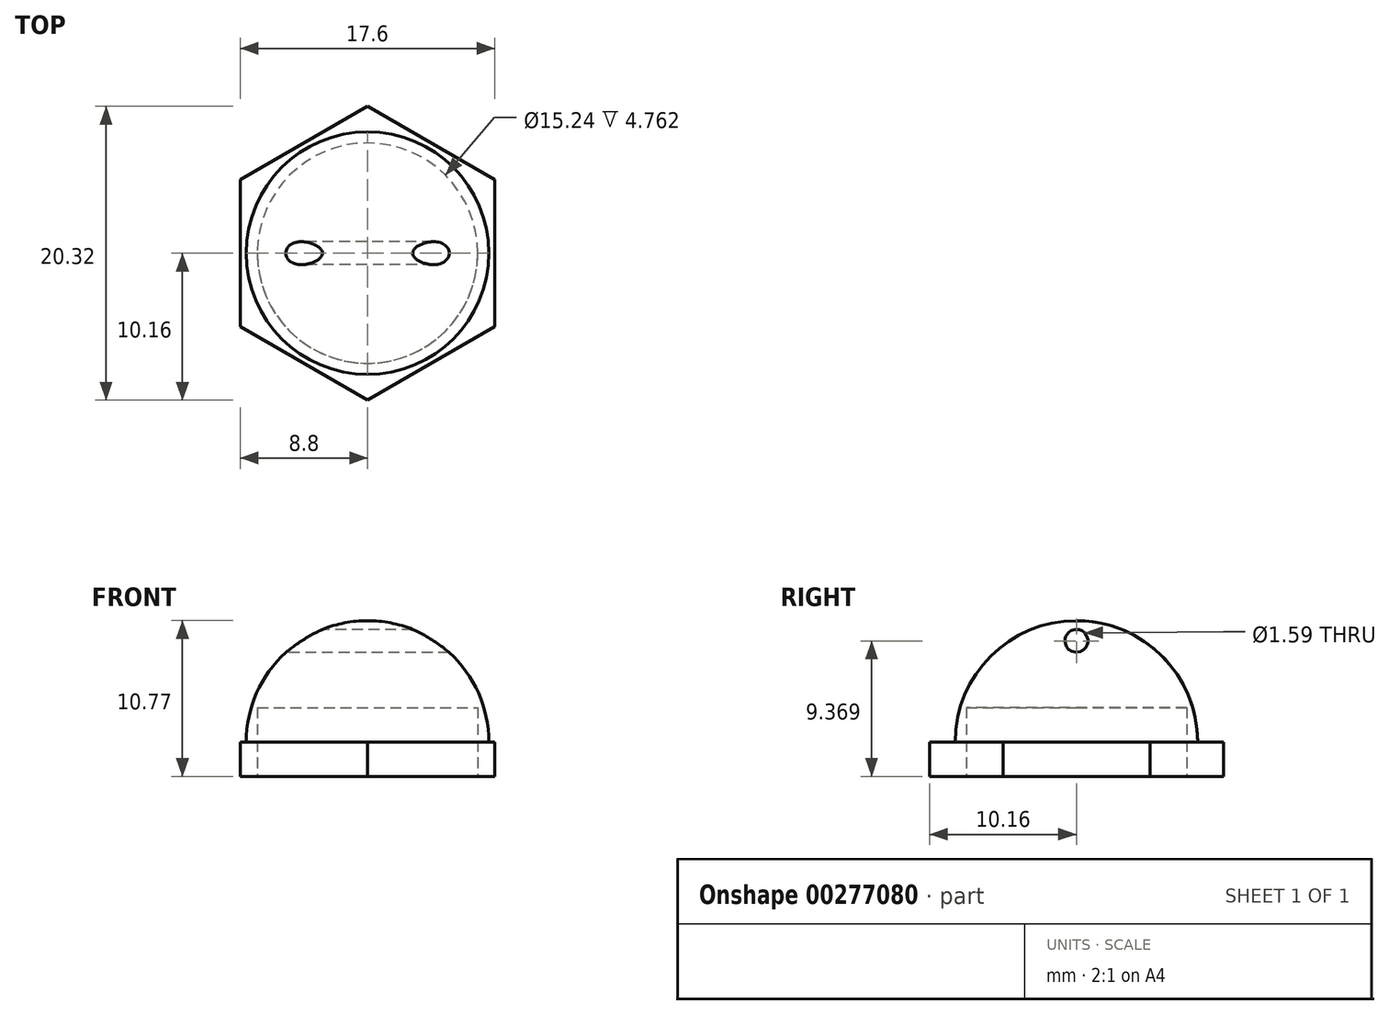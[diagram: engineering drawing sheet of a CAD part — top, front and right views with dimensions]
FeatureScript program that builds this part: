
annotation { "Feature Type Name" : "Feature", "Feature Type Description" : "" }
export const myFeature = defineFeature(function(context is Context, id is Id, definition is map)
    precondition{}
    {
        {
            var Q0;
            Q0=qCreatedBy(makeId("Top.planeOp"),FACE);
            var sketch = newSketch(context, id + "F0", { "sketchPlane" : qUnion([Q0])});
            skCircle(sketch, "E0.cCircle", {"center": v(0, 0) * mm, "radius": 10.16 * mm, "construction": true});
            skLineSegment(sketch, "E0.0", {"start": v(0, 10.16) * mm, "end": v(8.8, 5.08) * mm});
            skLineSegment(sketch, "E0.1", {"start": v(8.8, 5.08) * mm, "end": v(8.8, -5.08) * mm});
            skLineSegment(sketch, "E0.2", {"start": v(8.8, -5.08) * mm, "end": v(0, -10.16) * mm});
            skLineSegment(sketch, "E0.3", {"start": v(0, -10.16) * mm, "end": v(-8.8, -5.08) * mm});
            skLineSegment(sketch, "E0.4", {"start": v(-8.8, -5.08) * mm, "end": v(-8.8, 5.08) * mm});
            skLineSegment(sketch, "E0.5", {"start": v(-8.8, 5.08) * mm, "end": v(0, 10.16) * mm});
            skSolve(sketch);
        }
        {
            var Q0;
            Q0=qSketchRegion(id+"F0",true);
            extrude(context, id + "F1", {"entities" : qUnion([Q0]), "depth" : 7.94 * mm});
        }
        {
            var Q0;
            Q0=makeQuery(id+"F1.opExtrude","CAP_FACE",FACE,{"disambiguationData":[OSD([sQuery(id+"F0.wireOp",EDGE,"E0.0"),sQuery(id+"F0.wireOp",EDGE,"E0.1"),sQuery(id+"F0.wireOp",EDGE,"E0.2"),sQuery(id+"F0.wireOp",EDGE,"E0.3"),sQuery(id+"F0.wireOp",EDGE,"E0.4"),sQuery(id+"F0.wireOp",EDGE,"E0.5")])],"isStart":false});
            var sketch = newSketch(context, id + "F2", { "sketchPlane" : qUnion([Q0])});
            skCircle(sketch, "E1.cCircle", {"center": v(0, 0) * mm, "radius": 8.26 * mm, "construction": true});
            skLineSegment(sketch, "E1.0", {"start": v(0, 8.26) * mm, "end": v(1.27, 7.52) * mm});
            skLineSegment(sketch, "E1.1", {"start": v(7.15, 4.13) * mm, "end": v(7.15, 2.66) * mm});
            skLineSegment(sketch, "E1.2", {"start": v(7.15, -4.13) * mm, "end": v(5.88, -4.86) * mm});
            skLineSegment(sketch, "E1.3", {"start": v(0, -8.26) * mm, "end": v(-1.27, -7.52) * mm});
            skLineSegment(sketch, "E1.4", {"start": v(-7.15, -4.13) * mm, "end": v(-7.15, -2.66) * mm});
            skLineSegment(sketch, "E1.5", {"start": v(-7.15, 4.13) * mm, "end": v(-5.88, 4.86) * mm});
            skLineSegment(sketch, "E2", {"start": v(-1.27, 7.52) * mm, "end": v(1.27, 7.52) * mm});
            skLineSegment(sketch, "E3", {"start": v(-5.88, 4.86) * mm, "end": v(-7.15, 2.66) * mm});
            skLineSegment(sketch, "E4", {"start": v(-7.15, -2.66) * mm, "end": v(-5.88, -4.86) * mm});
            skLineSegment(sketch, "E5", {"start": v(-1.27, -7.52) * mm, "end": v(1.27, -7.52) * mm});
            skLineSegment(sketch, "E6", {"start": v(5.88, -4.86) * mm, "end": v(7.15, -2.66) * mm});
            skLineSegment(sketch, "E7", {"start": v(7.15, 2.66) * mm, "end": v(5.88, 4.86) * mm});
            skLineSegment(sketch, "E8.trimOffspring", {"start": v(-7.15, 2.66) * mm, "end": v(-7.15, 4.13) * mm});
            skLineSegment(sketch, "E9.trimOffspring", {"start": v(-5.88, -4.86) * mm, "end": v(-7.15, -4.13) * mm});
            skLineSegment(sketch, "E10.trimOffspring", {"start": v(1.27, -7.52) * mm, "end": v(0, -8.25) * mm});
            skLineSegment(sketch, "E11.trimOffspring", {"start": v(7.15, -2.66) * mm, "end": v(7.15, -4.13) * mm});
            skLineSegment(sketch, "E12.trimOffspring", {"start": v(5.88, 4.86) * mm, "end": v(7.15, 4.13) * mm});
            skLineSegment(sketch, "E13.trimOffspring", {"start": v(-1.27, 7.52) * mm, "end": v(0, 8.25) * mm});
            skCircle(sketch, "E14", {"center": v(0, 0) * mm, "radius": 7.52 * mm, "construction": true});
            skSolve(sketch);
        }
        {
            var Q0;
            Q0=qSketchRegion(id+"F2",true);
            extrude(context, id + "F3", {"entities" : qUnion([Q0]), "operationType" : NewBodyOperationType.ADD, "depth" : 22.22 * mm});
        }
        {
            var Q0;
            Q0=makeQuery(id+"F3.opExtrude","CAP_FACE",FACE,{"disambiguationData":[OSD([sQuery(id+"F2.wireOp",EDGE,"E1.0"),sQuery(id+"F2.wireOp",EDGE,"E2"),sQuery(id+"F2.wireOp",EDGE,"E13.trimOffspring")])],"isStart":false});
            var sketch = newSketch(context, id + "F4", { "sketchPlane" : qUnion([Q0])});
            skCircle(sketch, "E15.cCircle", {"center": v(0, 0) * mm, "radius": 10.16 * mm, "construction": true});
            skLineSegment(sketch, "E15.0", {"start": v(0, 10.16) * mm, "end": v(8.8, 5.08) * mm});
            skLineSegment(sketch, "E15.1", {"start": v(8.8, 5.08) * mm, "end": v(8.8, -5.08) * mm});
            skLineSegment(sketch, "E15.2", {"start": v(8.8, -5.08) * mm, "end": v(0, -10.16) * mm});
            skLineSegment(sketch, "E15.3", {"start": v(0, -10.16) * mm, "end": v(-8.8, -5.08) * mm});
            skLineSegment(sketch, "E15.4", {"start": v(-8.8, -5.08) * mm, "end": v(-8.8, 5.08) * mm});
            skLineSegment(sketch, "E15.5", {"start": v(-8.8, 5.08) * mm, "end": v(0, 10.16) * mm});
            skCircle(sketch, "E16", {"center": v(0, 0) * mm, "radius": 7.62 * mm});
            skSolve(sketch);
        }
        {
            var Q0;
            Q0=qSketchRegion(id+"F4",true);
            extrude(context, id + "F5", {"entities" : qUnion([Q0]), "operationType" : NewBodyOperationType.ADD, "depth" : 2.38 * mm});
        }
        {
            var Q0;
            Q0=qCreatedBy(makeId("Right.planeOp"),FACE);
            var sketch = newSketch(context, id + "F6", { "sketchPlane" : qUnion([Q0])});
            skLineSegment(sketch, "E17", {"start": v(0, 34.93) * mm, "end": v(-7.62, 34.93) * mm});
            skLineSegment(sketch, "E18", {"start": v(-7.62, 34.93) * mm, "end": v(-7.62, 32.54) * mm});
            skArc(sketch, "E19", {"start": v(0, 40.93) * mm, "mid": v(-5.93, 38.47) * mm, "end": v(-8.38, 32.54) * mm});
            skLineSegment(sketch, "E20", {"start": v(0, 40.93) * mm, "end": v(0, 34.93) * mm});
            skLineSegment(sketch, "E21", {"start": v(-8.38, 32.54) * mm, "end": v(-7.62, 32.54) * mm});
            skSolve(sketch);
        }
        {
            var Q0;
            Q0=qSketchRegion(id+"F6",true);
            var Q1;
            Q1=makeQuery(id+"F5.opExtrude","CAP_EDGE",EDGE,{"disambiguationData":[OSD([sQuery(id+"F4.wireOp",EDGE,"E16")])],"isStart":false});
            revolve(context, id + "F7", {"operationType" : NewBodyOperationType.ADD, "entities" : qUnion([Q0]), "axis" : qUnion([Q1]), "revolveType" : RevolveType.FULL});
        }
        {
            var Q0;
            Q0=makeQuery(id+"F1.opExtrude","CAP_FACE",FACE,{"disambiguationData":[OSD([sQuery(id+"F0.wireOp",EDGE,"E0.0"),sQuery(id+"F0.wireOp",EDGE,"E0.1"),sQuery(id+"F0.wireOp",EDGE,"E0.2"),sQuery(id+"F0.wireOp",EDGE,"E0.3"),sQuery(id+"F0.wireOp",EDGE,"E0.4"),sQuery(id+"F0.wireOp",EDGE,"E0.5")])],"isStart":true});
            var sketch = newSketch(context, id + "F8", { "sketchPlane" : qUnion([Q0])});
            skCircle(sketch, "E22", {"center": v(0, 0) * mm, "radius": 6.8 * mm});
            skSolve(sketch);
        }
        {
            var Q0;
            Q0=qSketchRegion(id+"F8",true);
            extrude(context, id + "F9", {"entities" : qUnion([Q0]), "operationType" : NewBodyOperationType.REMOVE, "oppositeDirection" : true, "depth" : 4.76 * mm});
        }
        {
            var Q0;
            Q0=makeQuery(id+"F9.boolean.opBoolean","COPY",FACE,{"derivedFrom":makeQuery(id+"F9.opExtrude","CAP_FACE",FACE,{"disambiguationData":[OSD([sQuery(id+"F8.wireOp",EDGE,"E22")])],"isStart":false})});
            var sketch = newSketch(context, id + "F10", { "sketchPlane" : qUnion([Q0])});
            skCircle(sketch, "E23", {"center": v(0, 0) * mm, "radius": 6.35 * mm});
            skSolve(sketch);
        }
        {
            var Q0;
            Q0=qSketchRegion(id+"F10",true);
            extrude(context, id + "F11", {"entities" : qUnion([Q0]), "operationType" : NewBodyOperationType.REMOVE, "endBound" : BoundingType.UP_TO_NEXT, "oppositeDirection" : true, "depth" : 25.4 * mm});
        }
        {
            var Q0;
            Q0=makeQuery(id+"F1.opExtrude","CAP_FACE",FACE,{"disambiguationData":[OSD([sQuery(id+"F0.wireOp",EDGE,"E0.0"),sQuery(id+"F0.wireOp",EDGE,"E0.1"),sQuery(id+"F0.wireOp",EDGE,"E0.2"),sQuery(id+"F0.wireOp",EDGE,"E0.3"),sQuery(id+"F0.wireOp",EDGE,"E0.4"),sQuery(id+"F0.wireOp",EDGE,"E0.5")])],"isStart":true});
            var sketch = newSketch(context, id + "F12", { "sketchPlane" : qUnion([Q0])});
            skCircle(sketch, "E24", {"center": v(0, 0) * mm, "radius": 6.8 * mm});
            skCircle(sketch, "E25.cCircle", {"center": v(0, 0) * mm, "radius": 8.57 * mm, "construction": true});
            skLineSegment(sketch, "E25.0", {"start": v(0, -8.57) * mm, "end": v(-7.42, -4.29) * mm});
            skLineSegment(sketch, "E25.1", {"start": v(-7.42, -4.29) * mm, "end": v(-7.42, 4.29) * mm});
            skLineSegment(sketch, "E25.2", {"start": v(-7.42, 4.29) * mm, "end": v(0, 8.57) * mm});
            skLineSegment(sketch, "E25.3", {"start": v(0, 8.57) * mm, "end": v(7.42, 4.29) * mm});
            skLineSegment(sketch, "E25.4", {"start": v(7.42, 4.29) * mm, "end": v(7.42, -4.29) * mm});
            skLineSegment(sketch, "E25.5", {"start": v(7.42, -4.29) * mm, "end": v(0, -8.57) * mm});
            skSolve(sketch);
        }
        {
            var Q0;
            Q0=qSketchRegion(id+"F12",true);
            extrude(context, id + "F13", {"entities" : qUnion([Q0]), "operationType" : NewBodyOperationType.ADD, "depth" : 3.17 * mm});
        }
        {
            var Q0;
            Q0=qCreatedBy(makeId("Right.planeOp"),FACE);
            var sketch = newSketch(context, id + "F14", { "sketchPlane" : qUnion([Q0])});
            skCircle(sketch, "E26", {"center": v(0, 39.53) * mm, "radius": 0.8 * mm});
            skSolve(sketch);
        }
        {
            var Q0;
            Q0=qSketchRegion(id+"F14",true);
            extrude(context, id + "F15", {"entities" : qUnion([Q0]), "operationType" : NewBodyOperationType.REMOVE, "endBound" : BoundingType.THROUGH_ALL, "depth" : 0.8 * mm, "hasSecondDirection" : true, "secondDirectionBound" : SecondDirectionBoundingType.THROUGH_ALL, "secondDirectionOppositeDirection" : true, "secondDirectionDepth" : 0.8 * mm});
        }
        {
            var Q0;
            Q0=makeQuery(id+"F13.opExtrude","CAP_FACE",FACE,{"disambiguationData":[OSD([sQuery(id+"F12.wireOp",EDGE,"E24"),sQuery(id+"F12.wireOp",EDGE,"E25.0"),sQuery(id+"F12.wireOp",EDGE,"E25.1"),sQuery(id+"F12.wireOp",EDGE,"E25.2"),sQuery(id+"F12.wireOp",EDGE,"E25.3"),sQuery(id+"F12.wireOp",EDGE,"E25.4"),sQuery(id+"F12.wireOp",EDGE,"E25.5")])],"isStart":false});
            var sketch = newSketch(context, id + "F16", { "sketchPlane" : qUnion([Q0])});
            skCircle(sketch, "E27", {"center": v(0, 0) * mm, "radius": 12.41 * mm});
            skSolve(sketch);
        }
        {
            var Q0;
            Q0 = qSketchRegion(id + "F16", true);
            var Q1;
            Q1=makeQuery(id+"F5.opExtrude","CAP_FACE",FACE,{"disambiguationData":[OSD([sQuery(id+"F4.wireOp",EDGE,"E15.0"),sQuery(id+"F4.wireOp",EDGE,"E15.1"),sQuery(id+"F4.wireOp",EDGE,"E15.2"),sQuery(id+"F4.wireOp",EDGE,"E15.3"),sQuery(id+"F4.wireOp",EDGE,"E15.4"),sQuery(id+"F4.wireOp",EDGE,"E15.5"),sQuery(id+"F4.wireOp",EDGE,"E16")])],"isStart":true});
            extrude(context, id + "F17", {"entities" : qUnion([Q0]), "operationType" : NewBodyOperationType.REMOVE, "endBound" : BoundingType.UP_TO_SURFACE, "oppositeDirection" : true, "endBoundEntityFace" : qUnion([Q1]), "depth" : 25.4 * mm});
        }
    });
